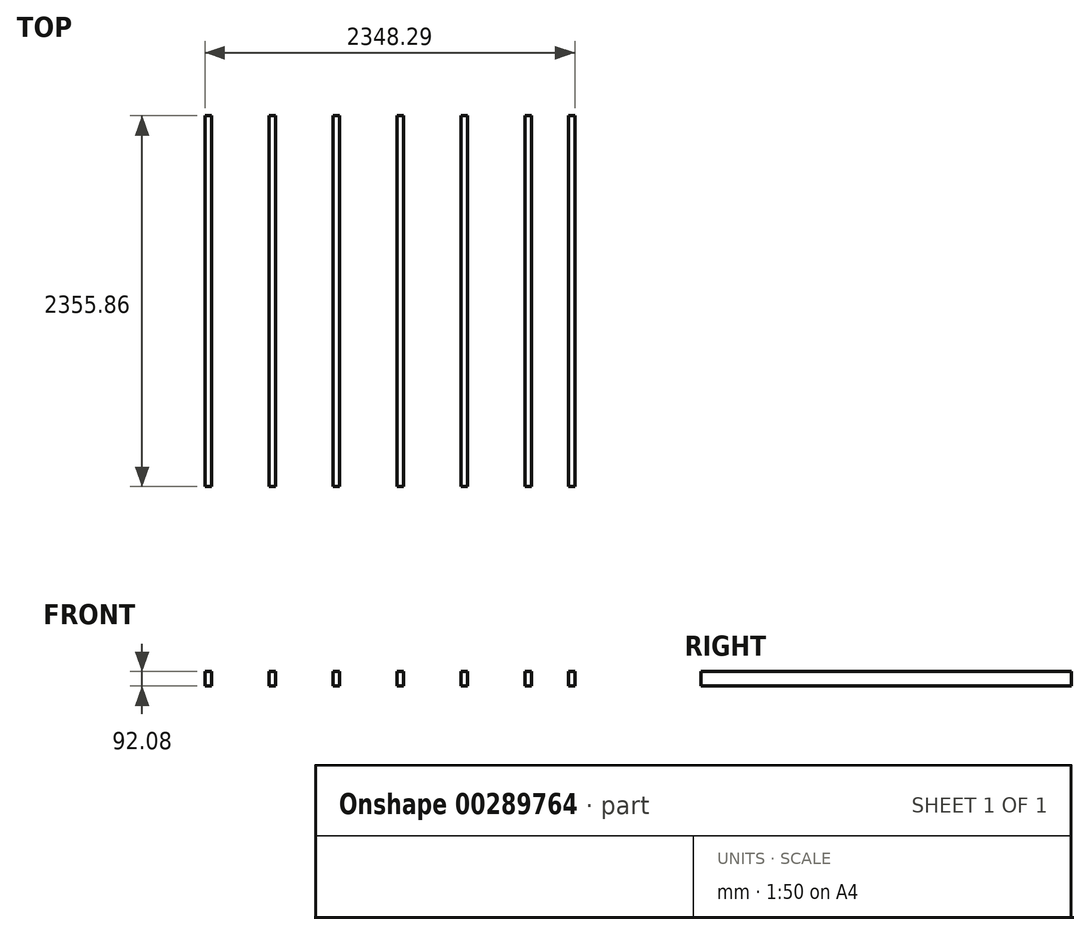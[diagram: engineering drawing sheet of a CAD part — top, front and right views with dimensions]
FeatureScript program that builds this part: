
annotation { "Feature Type Name" : "Feature", "Feature Type Description" : "" }
export const myFeature = defineFeature(function(context is Context, id is Id, definition is map)
    precondition{}
    {
        {
            var Q0;
            Q0=qCreatedBy(makeId("Top.planeOp"),FACE);
            var sketch = newSketch(context, id + "F0", { "sketchPlane" : qUnion([Q0])});
            skLineSegment(sketch, "E0.bottom", {"start": v(4068.78, -1219.2) * mm, "end": v(-4068.78, -1219.2) * mm});
            skLineSegment(sketch, "E0.top", {"start": v(4068.78, 1219.2) * mm, "end": v(-4068.78, 1219.2) * mm});
            skLineSegment(sketch, "E0.left", {"start": v(4068.78, -1219.2) * mm, "end": v(4068.78, 1219.2) * mm});
            skLineSegment(sketch, "E0.right", {"start": v(-4068.78, -1219.2) * mm, "end": v(-4068.78, 1219.2) * mm});
            skPoint(sketch, "E0.middle", {"position": v(0, 0) * mm});
            skLineSegment(sketch, "E1.bottom", {"start": v(-4068.78, -1219.2) * mm, "end": v(4068.78, -1219.2) * mm});
            skLineSegment(sketch, "E1.top", {"start": v(-4068.78, -1177.93) * mm, "end": v(4068.78, -1177.93) * mm});
            skLineSegment(sketch, "E1.left", {"start": v(-4068.78, -1219.2) * mm, "end": v(-4068.78, -1177.93) * mm});
            skLineSegment(sketch, "E1.right", {"start": v(4068.78, -1219.2) * mm, "end": v(4068.78, -1177.93) * mm});
            skLineSegment(sketch, "E2.bottom", {"start": v(-4068.78, 1219.2) * mm, "end": v(4068.78, 1219.2) * mm});
            skLineSegment(sketch, "E2.top", {"start": v(-4068.78, 1177.93) * mm, "end": v(4068.78, 1177.93) * mm});
            skLineSegment(sketch, "E2.left", {"start": v(-4068.78, 1219.2) * mm, "end": v(-4068.78, 1177.93) * mm});
            skLineSegment(sketch, "E2.right", {"start": v(4068.78, 1219.2) * mm, "end": v(4068.78, 1177.93) * mm});
            skLineSegment(sketch, "E3.bottom", {"start": v(-4068.78, 1177.93) * mm, "end": v(-4027.5, 1177.93) * mm});
            skLineSegment(sketch, "E3.top", {"start": v(-4068.78, -1177.93) * mm, "end": v(-4027.5, -1177.93) * mm});
            skLineSegment(sketch, "E3.left", {"start": v(-4068.78, 1177.93) * mm, "end": v(-4068.78, -1177.93) * mm});
            skLineSegment(sketch, "E3.right", {"start": v(-4027.5, 1177.93) * mm, "end": v(-4027.5, -1177.93) * mm});
            skLineSegment(sketch, "E4.bottom", {"start": v(-3662.38, 1177.93) * mm, "end": v(-3621.1, 1177.93) * mm});
            skLineSegment(sketch, "E4.top", {"start": v(-3662.38, -1177.93) * mm, "end": v(-3621.1, -1177.93) * mm});
            skLineSegment(sketch, "E4.left", {"start": v(-3662.38, 1177.93) * mm, "end": v(-3662.38, -1177.93) * mm});
            skLineSegment(sketch, "E4.right", {"start": v(-3621.1, 1177.93) * mm, "end": v(-3621.1, -1177.93) * mm});
            skLineSegment(sketch, "E5", {"start": v(-3641.74, 1177.93) * mm, "end": v(-3641.74, -1177.93) * mm, "construction": true});
            skLineSegment(sketch, "E6", {"start": v(-4048.14, 1177.93) * mm, "end": v(-4048.14, -1177.93) * mm, "construction": true});
            skLineSegment(sketch, "E7.MirrorCS", {"start": v(-3255.98, 1177.93) * mm, "end": v(-3255.98, -1177.93) * mm});
            skLineSegment(sketch, "E8.MirrorCS", {"start": v(-3214.7, -1219.2) * mm, "end": v(-3214.7, 1219.2) * mm});
            skLineSegment(sketch, "E9.MirrorCS", {"start": v(-3235.34, 1177.93) * mm, "end": v(-3235.34, -1177.93) * mm, "construction": true});
            skLineSegment(sketch, "E10.MirrorCS", {"start": v(-2849.58, 1177.93) * mm, "end": v(-2849.58, -1177.93) * mm});
            skLineSegment(sketch, "E11.MirrorCS", {"start": v(-2808.3, 1177.93) * mm, "end": v(-2808.3, -1177.93) * mm});
            skLineSegment(sketch, "E12.MirrorCS", {"start": v(-2443.18, 1177.93) * mm, "end": v(-2443.18, -1177.93) * mm});
            skLineSegment(sketch, "E13.MirrorCS", {"start": v(-2422.54, 1177.93) * mm, "end": v(-2422.54, -1177.93) * mm, "construction": true});
            skLineSegment(sketch, "E14.MirrorCS", {"start": v(-2401.9, -1219.2) * mm, "end": v(-2401.9, 1219.2) * mm});
            skLineSegment(sketch, "E15.MirrorCS", {"start": v(-2036.78, 1177.93) * mm, "end": v(-2036.78, -1177.93) * mm});
            skLineSegment(sketch, "E16.MirrorCS", {"start": v(-1995.5, 1177.93) * mm, "end": v(-1995.5, -1177.93) * mm});
            skLineSegment(sketch, "E17.MirrorCS", {"start": v(-1630.38, -1219.2) * mm, "end": v(-1630.38, 1219.2) * mm});
            skLineSegment(sketch, "E18.MirrorCS", {"start": v(-1589.1, 1177.93) * mm, "end": v(-1589.1, -1177.93) * mm});
            skLineSegment(sketch, "E19.MirrorCS", {"start": v(-1223.98, 1177.93) * mm, "end": v(-1223.98, -1177.93) * mm});
            skLineSegment(sketch, "E20.MirrorCS", {"start": v(-1182.7, 1177.93) * mm, "end": v(-1182.7, -1177.93) * mm});
            skLineSegment(sketch, "E21.MirrorCS", {"start": v(-817.58, 1177.93) * mm, "end": v(-817.58, -1177.93) * mm});
            skLineSegment(sketch, "E22.MirrorCS", {"start": v(-776.3, -1219.2) * mm, "end": v(-776.3, 1219.2) * mm});
            skLineSegment(sketch, "E23.MirrorCS", {"start": v(-796.94, 1177.93) * mm, "end": v(-796.94, -1177.93) * mm, "construction": true});
            skLineSegment(sketch, "E24.MirrorCS", {"start": v(-411.18, 1177.93) * mm, "end": v(-411.18, -1177.93) * mm});
            skLineSegment(sketch, "E25.MirrorCS", {"start": v(-369.9, 1177.93) * mm, "end": v(-369.9, -1177.93) * mm});
            skLineSegment(sketch, "E26.MirrorCS", {"start": v(-4.78, 1177.93) * mm, "end": v(-4.78, -1177.93) * mm});
            skLineSegment(sketch, "E27.MirrorCS", {"start": v(36.5, -1219.2) * mm, "end": v(36.5, 1219.2) * mm});
            skLineSegment(sketch, "E28.MirrorCS", {"start": v(401.62, 1177.93) * mm, "end": v(401.62, -1177.93) * mm});
            skLineSegment(sketch, "E29.MirrorCS", {"start": v(442.9, 1177.93) * mm, "end": v(442.9, -1177.93) * mm});
            skLineSegment(sketch, "E30.MirrorCS", {"start": v(808.02, -1219.2) * mm, "end": v(808.02, 1219.2) * mm});
            skLineSegment(sketch, "E31.MirrorCS", {"start": v(849.3, 1177.93) * mm, "end": v(849.3, -1177.93) * mm});
            skLineSegment(sketch, "E32.MirrorCS", {"start": v(1662.1, 1177.93) * mm, "end": v(1662.1, -1177.93) * mm});
            skLineSegment(sketch, "E33.MirrorCS", {"start": v(2027.22, 1177.93) * mm, "end": v(2027.22, -1177.93) * mm});
            skLineSegment(sketch, "E34.MirrorCS", {"start": v(2068.5, 1177.93) * mm, "end": v(2068.5, -1177.93) * mm});
            skLineSegment(sketch, "E35.MirrorCS", {"start": v(2433.62, 1177.93) * mm, "end": v(2433.62, -1177.93) * mm});
            skLineSegment(sketch, "E36.MirrorCS", {"start": v(2454.26, 1177.93) * mm, "end": v(2454.26, -1177.93) * mm, "construction": true});
            skLineSegment(sketch, "E37.MirrorCS", {"start": v(2474.9, -1219.2) * mm, "end": v(2474.9, 1219.2) * mm});
            skLineSegment(sketch, "E38.MirrorCS", {"start": v(2840.02, 1177.93) * mm, "end": v(2840.02, -1177.93) * mm});
            skLineSegment(sketch, "E39.MirrorCS", {"start": v(2881.3, 1177.93) * mm, "end": v(2881.3, -1177.93) * mm});
            skLineSegment(sketch, "E40.MirrorCS", {"start": v(3246.42, 1177.93) * mm, "end": v(3246.42, -1177.93) * mm});
            skLineSegment(sketch, "E41.bottom", {"start": v(4068.78, 1177.93) * mm, "end": v(4027.5, 1177.93) * mm});
            skLineSegment(sketch, "E41.top", {"start": v(4068.78, -1177.93) * mm, "end": v(4027.5, -1177.93) * mm});
            skLineSegment(sketch, "E41.left", {"start": v(4068.78, 1177.93) * mm, "end": v(4068.78, -1177.93) * mm});
            skLineSegment(sketch, "E41.right", {"start": v(4027.5, 1177.93) * mm, "end": v(4027.5, -1177.93) * mm});
            skLineSegment(sketch, "E42", {"start": v(1214.45, 1177.93) * mm, "end": v(1214.45, -1177.93) * mm});
            skLineSegment(sketch, "E43", {"start": v(1255.73, 1177.93) * mm, "end": v(1255.73, -1219.2) * mm});
            skLineSegment(sketch, "E44", {"start": v(1620.82, 1177.93) * mm, "end": v(1620.82, -1177.93) * mm});
            skLineSegment(sketch, "E45.MirrorCS", {"start": v(3287.7, 1177.93) * mm, "end": v(3287.7, -1177.93) * mm});
            skLineSegment(sketch, "E46.MirrorCS", {"start": v(3652.8, 1177.93) * mm, "end": v(3652.8, -1219.2) * mm});
            skLineSegment(sketch, "E47.MirrorCS", {"start": v(3694.07, 1177.93) * mm, "end": v(3694.07, -1177.93) * mm});
            skLineSegment(sketch, "E48", {"start": v(-907.7, 1219.2) * mm, "end": v(-907.7, -1219.2) * mm});
            skLineSegment(sketch, "E49", {"start": v(-948.84, 1219.2) * mm, "end": v(-948.84, -1219.2) * mm});
            skSolve(sketch);
        }
        {
            var Q0;
            {var subQ0=sQuery(id+"F0.wireOp",EDGE,"E7.MirrorCS");Q0=makeQuery(id+"F0.imprint","IMPRINT",FACE,{"disambiguationData":[TD([[makeQuery(id+"F0.imprint","IMPRINT",EDGE,{"derivedFrom":subQ0}),1.0]])]});}
            var Q1;
            {var subQ0=sQuery(id+"F0.wireOp",EDGE,"E10.MirrorCS");Q1=makeQuery(id+"F0.imprint","IMPRINT",FACE,{"disambiguationData":[TD([[makeQuery(id+"F0.imprint","IMPRINT",EDGE,{"derivedFrom":subQ0}),1.0]])]});}
            var Q2;
            {var subQ0=sQuery(id+"F0.wireOp",EDGE,"E12.MirrorCS");Q2=makeQuery(id+"F0.imprint","IMPRINT",FACE,{"disambiguationData":[TD([[makeQuery(id+"F0.imprint","IMPRINT",EDGE,{"derivedFrom":subQ0}),1.0]])]});}
            var Q3;
            {var subQ0=sQuery(id+"F0.wireOp",EDGE,"E15.MirrorCS");Q3=makeQuery(id+"F0.imprint","IMPRINT",FACE,{"disambiguationData":[TD([[makeQuery(id+"F0.imprint","IMPRINT",EDGE,{"derivedFrom":subQ0}),1.0]])]});}
            var Q4;
            {var subQ0=sQuery(id+"F0.wireOp",EDGE,"E18.MirrorCS");Q4=makeQuery(id+"F0.imprint","IMPRINT",FACE,{"disambiguationData":[TD([[makeQuery(id+"F0.imprint","IMPRINT",EDGE,{"derivedFrom":subQ0}),-1.0]])]});}
            var Q5;
            {var subQ0=sQuery(id+"F0.wireOp",EDGE,"E19.MirrorCS");Q5=makeQuery(id+"F0.imprint","IMPRINT",FACE,{"disambiguationData":[TD([[makeQuery(id+"F0.imprint","IMPRINT",EDGE,{"derivedFrom":subQ0}),1.0]])]});}
            var Q6;
            {var subQ0=sQuery(id+"F0.wireOp",EDGE,"E49");var subQ1=sQuery(id+"F0.wireOp",EDGE,"E1.top");var subQ2=makeQuery(id+"F0.imprint","INTERSECT",VERTEX,{"derivedFrom":[subQ1,subQ0]});Q6=makeQuery(id+"F0.imprint","IMPRINT",FACE,{"disambiguationData":[TD([[makeQuery(id+"F0.imprint","IMPRINT",EDGE,{"disambiguationData":[TD([[subQ2,-1.0]])],"derivedFrom":subQ1}),1.0]])]});}
            var Q7;
            Q7=makeQuery(id+"F0.imprint","IMPRINT",FACE,{"disambiguationData":[TD([[makeQuery(id+"F0.imprint","IMPRINT",EDGE,{"derivedFrom":sQuery(id+"F0.wireOp",EDGE,"E3.bottom")}),-1.0]])]});
            var Q8;
            {var subQ5=sQuery(id+"F0.wireOp",EDGE,"E14.MirrorCS");var subQ7=sQuery(id+"F0.wireOp",EDGE,"E1.bottom");var subQ8=makeQuery(id+"F0.imprint","INTERSECT",VERTEX,{"derivedFrom":[subQ7,subQ5]});Q8=makeQuery(id+"F0.imprint","IMPRINT",FACE,{"disambiguationData":[TD([[makeQuery(id+"F0.imprint","IMPRINT",EDGE,{"disambiguationData":[TD([[subQ8,-1.0]])],"derivedFrom":subQ7}),1.0]])]});}
            var Q9;
            {var subQ4=sQuery(id+"F0.wireOp",EDGE,"E17.MirrorCS");var subQ6=sQuery(id+"F0.wireOp",EDGE,"E2.bottom");var subQ7=makeQuery(id+"F0.imprint","INTERSECT",VERTEX,{"derivedFrom":[subQ6,subQ4]});Q9=makeQuery(id+"F0.imprint","IMPRINT",FACE,{"disambiguationData":[TD([[makeQuery(id+"F0.imprint","IMPRINT",EDGE,{"disambiguationData":[TD([[subQ7,-1.0]])],"derivedFrom":subQ6}),-1.0]])]});}
            var Q10;
            {var subQ5=sQuery(id+"F0.wireOp",EDGE,"E2.left");Q10=makeQuery(id+"F0.imprint","IMPRINT",FACE,{"disambiguationData":[TD([[makeQuery(id+"F0.imprint","IMPRINT",EDGE,{"derivedFrom":subQ5}),1.0]])]});}
            var Q11;
            {var subQ6=sQuery(id+"F0.wireOp",EDGE,"E1.left");Q11=makeQuery(id+"F0.imprint","IMPRINT",FACE,{"disambiguationData":[TD([[makeQuery(id+"F0.imprint","IMPRINT",EDGE,{"derivedFrom":subQ6}),-1.0]])]});}
            var Q12;
            {var subQ4=sQuery(id+"F0.wireOp",EDGE,"E2.bottom");var subQ7=sQuery(id+"F0.wireOp",EDGE,"E14.MirrorCS");var subQ9=makeQuery(id+"F0.imprint","INTERSECT",VERTEX,{"derivedFrom":[subQ4,subQ7]});Q12=makeQuery(id+"F0.imprint","IMPRINT",FACE,{"disambiguationData":[TD([[makeQuery(id+"F0.imprint","IMPRINT",EDGE,{"disambiguationData":[TD([[subQ9,-1.0]])],"derivedFrom":subQ4}),-1.0]])]});}
            var Q13;
            {var subQ4=sQuery(id+"F0.wireOp",EDGE,"E17.MirrorCS");var subQ7=sQuery(id+"F0.wireOp",EDGE,"E1.bottom");var subQ10=makeQuery(id+"F0.imprint","INTERSECT",VERTEX,{"derivedFrom":[subQ7,subQ4]});Q13=makeQuery(id+"F0.imprint","IMPRINT",FACE,{"disambiguationData":[TD([[makeQuery(id+"F0.imprint","IMPRINT",EDGE,{"disambiguationData":[TD([[subQ10,-1.0]])],"derivedFrom":subQ7}),1.0]])]});}
            var Q14;
            {var subQ4=sQuery(id+"F0.wireOp",EDGE,"E8.MirrorCS");var subQ6=sQuery(id+"F0.wireOp",EDGE,"E1.bottom");var subQ7=makeQuery(id+"F0.imprint","INTERSECT",VERTEX,{"derivedFrom":[subQ6,subQ4]});Q14=makeQuery(id+"F0.imprint","IMPRINT",FACE,{"disambiguationData":[TD([[makeQuery(id+"F0.imprint","IMPRINT",EDGE,{"disambiguationData":[TD([[subQ7,-1.0]])],"derivedFrom":subQ6}),1.0]])]});}
            var Q15;
            {var subQ5=sQuery(id+"F0.wireOp",EDGE,"E2.bottom");var subQ8=sQuery(id+"F0.wireOp",EDGE,"E8.MirrorCS");var subQ10=makeQuery(id+"F0.imprint","INTERSECT",VERTEX,{"derivedFrom":[subQ5,subQ8]});Q15=makeQuery(id+"F0.imprint","IMPRINT",FACE,{"disambiguationData":[TD([[makeQuery(id+"F0.imprint","IMPRINT",EDGE,{"disambiguationData":[TD([[subQ10,-1.0]])],"derivedFrom":subQ5}),-1.0]])]});}
            var Q16;
            Q16=makeQuery(id+"F0.imprint","IMPRINT",FACE,{"disambiguationData":[TD([[makeQuery(id+"F0.imprint","IMPRINT",EDGE,{"derivedFrom":sQuery(id+"F0.wireOp",EDGE,"E4.bottom")}),-1.0]])]});
            var Q17;
            {var subQ0=sQuery(id+"F0.wireOp",EDGE,"E48");var subQ1=sQuery(id+"F0.wireOp",EDGE,"E1.bottom");var subQ2=makeQuery(id+"F0.imprint","INTERSECT",VERTEX,{"derivedFrom":[subQ1,subQ0]});Q17=makeQuery(id+"F0.imprint","IMPRINT",FACE,{"disambiguationData":[TD([[makeQuery(id+"F0.imprint","IMPRINT",EDGE,{"disambiguationData":[TD([[subQ2,1.0]])],"derivedFrom":subQ1}),1.0]])]});}
            var Q18;
            {var subQ0=sQuery(id+"F0.wireOp",EDGE,"E48");var subQ1=sQuery(id+"F0.wireOp",EDGE,"E2.bottom");var subQ2=makeQuery(id+"F0.imprint","INTERSECT",VERTEX,{"derivedFrom":[subQ1,subQ0]});Q18=makeQuery(id+"F0.imprint","IMPRINT",FACE,{"disambiguationData":[TD([[makeQuery(id+"F0.imprint","IMPRINT",EDGE,{"disambiguationData":[TD([[subQ2,1.0]])],"derivedFrom":subQ1}),-1.0]])]});}
            extrude(context, id + "F1", {"entities" : qUnion([Q0, Q1, Q2, Q3, Q4, Q5, Q6, Q7, Q8, Q9, Q10, Q11, Q12, Q13, Q14, Q15, Q16, Q17, Q18]), "depth" : 92.08 * mm});
        }
    });
